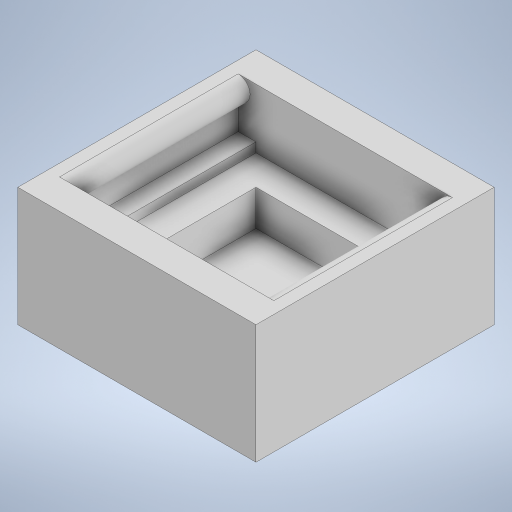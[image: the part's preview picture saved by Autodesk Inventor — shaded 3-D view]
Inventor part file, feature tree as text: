
AUTODESK INVENTOR PART (.ipt)
format: ipt  version: 2023 (Build 270158000, 158)  size: 281,600 bytes
history: native  units: in
note: dims shown in document units (in); Inventor stores cm internally (conversion verified against a paired STEP export)
features: extrude x4, sketch x4, plane x2, shell x1
ambient origin geometry x8: Origin, YZ Plane, XZ Plane, XY Plane, X Axis, Y Axis, Z Axis, Center Point
bodies: Solid1 (feature_tree)
feature tree (11):
  extrude  "Extrusion1"  Depth=1.0in
  shell  "Shell1"  Thickness=0.5in
  sketch  "Sketch2"  dims[d4=0.25in d5=0.75in]
  extrude  "Extrusion2"  Depth=0.75in
  extrude  "Extrusion3"  Depth=0.125in
  plane  "Work Plane1"
  plane  "Work Plane2"
  extrude  "Extrusion4"  Depth=0.4in TaperAngle=0.0deg
  sketch  "Sketch4"  dims[d8=0.125in d9=0.4in d10=0.0in d11=0.25in d12=0.0in d13=-0.5in d14=-0.5in d16=0.1in d17=0.05in d18=0.05in d20=0.1in d21=0.05in d22=0.05in d23=0.05in d24=0.21in d25=0.05in d26=0.21in d27=0.15in d28=0.21in d29=0.21in d30=0.15in d31=0.75in d32=0.0in d33=0.1in d34=0.1in d35=0.05in d36=0.05in d37=0.05in d38=0.05in d39=0.05in d40=0.15in d41=0.05in d42=0.15in d43=0.15in d44=0.15in d45=0.15in d46=0.15in d15=0.0in]
  sketch  "Sketch1"  dims[d0=1.0in d1=1.0in d2=0.5in d3=0.0in]
  sketch  "Sketch3"  dims[d6=0.75in d7=0.125in]
